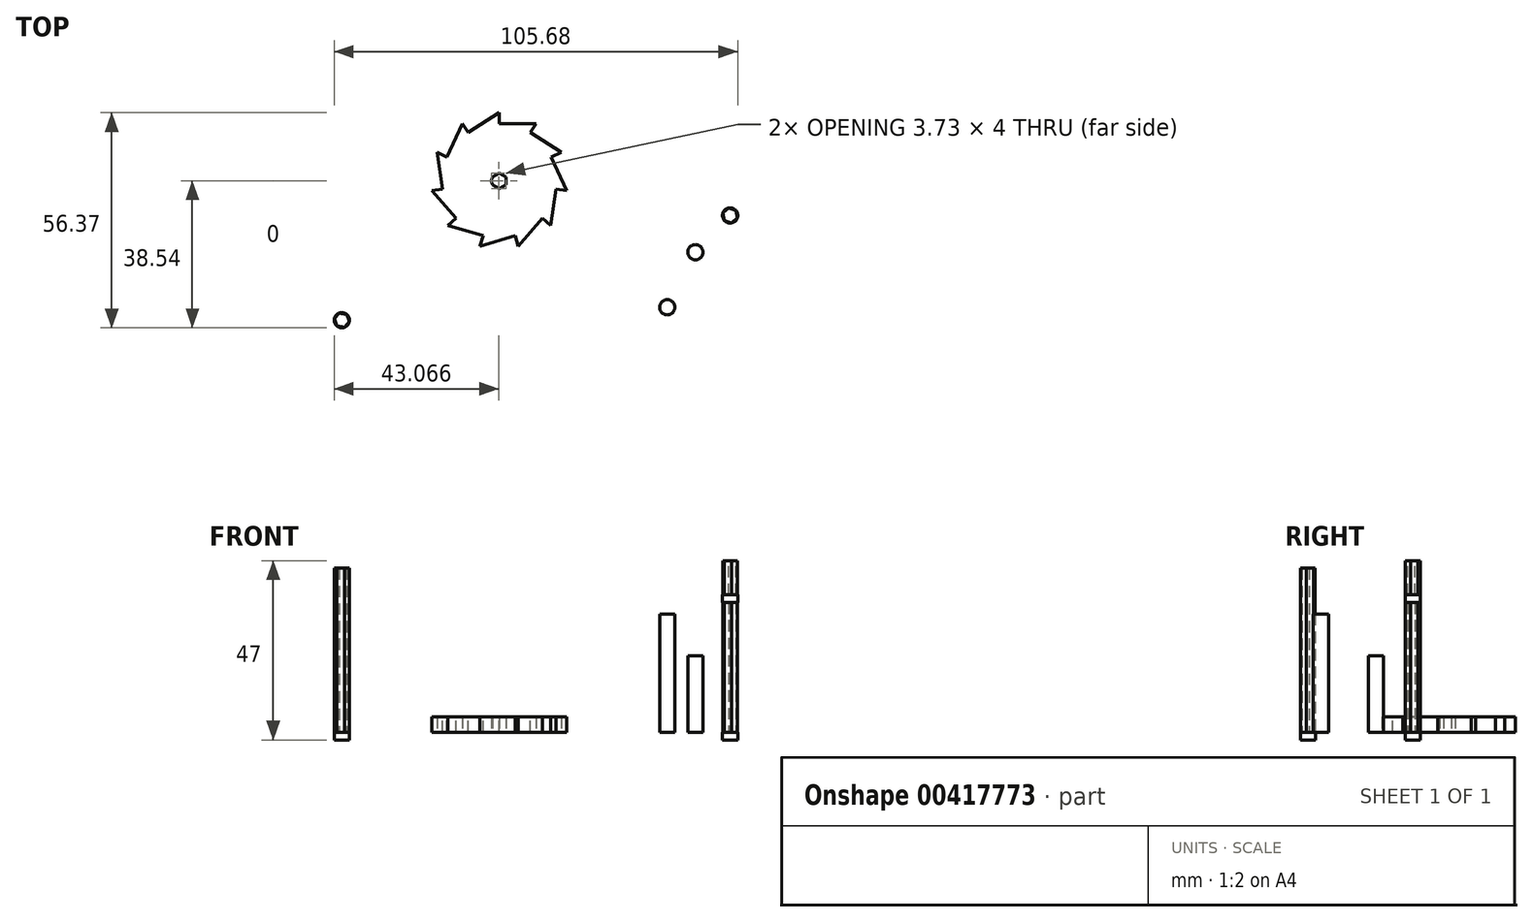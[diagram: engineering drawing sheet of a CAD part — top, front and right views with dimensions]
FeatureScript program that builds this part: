
annotation { "Feature Type Name" : "Feature", "Feature Type Description" : "" }
export const myFeature = defineFeature(function(context is Context, id is Id, definition is map)
    precondition{}
    {
        {
            var Q0;
            Q0=qCreatedBy(makeId("Top.planeOp"),FACE);
            var sketch = newSketch(context, id + "F0", { "sketchPlane" : qUnion([Q0])});
            skCircle(sketch, "E0", {"center": v(0, 0) * mm, "radius": 15 * mm});
            skLineSegment(sketch, "E1", {"start": v(0, -26.52) * mm, "end": v(0, 26.32) * mm});
            skLineSegment(sketch, "E2", {"start": v(-32.36, 0) * mm, "end": v(30.72, 0) * mm});
            skLineSegment(sketch, "E3", {"start": v(0, 15) * mm, "end": v(0, 17.83) * mm});
            skLineSegment(sketch, "E4", {"start": v(0, 17.83) * mm, "end": v(-8.1, 12.62) * mm});
            skLineSegment(sketch, "E5.1.0", {"start": v(-8.1, 12.62) * mm, "end": v(-9.64, 15) * mm});
            skLineSegment(sketch, "E5.1.1", {"start": v(-9.64, 15) * mm, "end": v(-13.64, 6.23) * mm});
            skLineSegment(sketch, "E5.2.0", {"start": v(-13.64, 6.23) * mm, "end": v(-16.22, 7.4) * mm});
            skLineSegment(sketch, "E5.2.1", {"start": v(-16.22, 7.4) * mm, "end": v(-14.85, -2.13) * mm});
            skLineSegment(sketch, "E5.3.0", {"start": v(-14.85, -2.13) * mm, "end": v(-17.65, -2.54) * mm});
            skLineSegment(sketch, "E5.3.1", {"start": v(-17.65, -2.54) * mm, "end": v(-11.34, -9.82) * mm});
            skLineSegment(sketch, "E5.4.0", {"start": v(-11.34, -9.82) * mm, "end": v(-13.48, -11.68) * mm});
            skLineSegment(sketch, "E5.4.1", {"start": v(-13.48, -11.68) * mm, "end": v(-4.23, -14.4) * mm});
            skLineSegment(sketch, "E5.5.0", {"start": v(-4.23, -14.4) * mm, "end": v(-5.02, -17.1) * mm});
            skLineSegment(sketch, "E5.5.1", {"start": v(-5.02, -17.1) * mm, "end": v(4.23, -14.4) * mm});
            skLineSegment(sketch, "E5.6.0", {"start": v(4.23, -14.4) * mm, "end": v(5.02, -17.1) * mm});
            skLineSegment(sketch, "E5.6.1", {"start": v(5.02, -17.1) * mm, "end": v(11.34, -9.82) * mm});
            skLineSegment(sketch, "E5.7.0", {"start": v(11.34, -9.82) * mm, "end": v(13.48, -11.68) * mm});
            skLineSegment(sketch, "E5.7.1", {"start": v(13.48, -11.68) * mm, "end": v(14.85, -2.13) * mm});
            skLineSegment(sketch, "E5.8.0", {"start": v(14.85, -2.13) * mm, "end": v(17.65, -2.54) * mm});
            skLineSegment(sketch, "E5.8.1", {"start": v(17.65, -2.54) * mm, "end": v(13.64, 6.23) * mm});
            skLineSegment(sketch, "E5.9.0", {"start": v(13.64, 6.23) * mm, "end": v(16.22, 7.4) * mm});
            skLineSegment(sketch, "E5.9.1", {"start": v(16.22, 7.4) * mm, "end": v(8.1, 12.62) * mm});
            skLineSegment(sketch, "E5.10.0", {"start": v(8.1, 12.62) * mm, "end": v(9.64, 15) * mm});
            skLineSegment(sketch, "E5.10.1", {"start": v(9.64, 15) * mm, "end": v(0, 15) * mm});
            skCircle(sketch, "E6.cCircle", {"center": v(0, 0) * mm, "radius": 1.73 * mm, "construction": true});
            skLineSegment(sketch, "E6.0", {"start": v(0, 2) * mm, "end": v(1.73, 1) * mm});
            skLineSegment(sketch, "E6.1", {"start": v(1.73, 1) * mm, "end": v(1.73, -1) * mm});
            skLineSegment(sketch, "E6.2", {"start": v(1.73, -1) * mm, "end": v(0, -2) * mm});
            skLineSegment(sketch, "E6.3", {"start": v(0, -2) * mm, "end": v(-1.73, -1) * mm});
            skLineSegment(sketch, "E6.4", {"start": v(-1.73, -1) * mm, "end": v(-1.73, 1) * mm});
            skLineSegment(sketch, "E6.5", {"start": v(-1.73, 1) * mm, "end": v(0, 2) * mm});
            skPoint(sketch, "E6.0.midPoint", {"position": v(0.87, 1.5) * mm});
            skCircle(sketch, "E7", {"center": v(0, 0) * mm, "radius": 2 * mm});
            skSolve(sketch);
        }
        {
            var Q0;
            Q0 = qSketchRegion(id + "F0", true);
            var Q1;
            {var subQ0=sQuery(id+"F0.wireOp",EDGE,"E6.5");Q1=makeQuery(id+"F0.imprint","IMPRINT",FACE,{"disambiguationData":[TD([[makeQuery(id+"F0.imprint","IMPRINT",EDGE,{"derivedFrom":subQ0}),1.0]])]});}
            var Q2;
            {var subQ0=sQuery(id+"F0.wireOp",EDGE,"E6.0");Q2=makeQuery(id+"F0.imprint","IMPRINT",FACE,{"disambiguationData":[TD([[makeQuery(id+"F0.imprint","IMPRINT",EDGE,{"derivedFrom":subQ0}),1.0]])]});}
            var Q3;
            {var subQ0=sQuery(id+"F0.wireOp",EDGE,"E6.1");var subQ1=sQuery(id+"F0.wireOp",EDGE,"E2");var subQ2=makeQuery(id+"F0.imprint","INTERSECT",VERTEX,{"derivedFrom":[subQ1,subQ0]});Q3=makeQuery(id+"F0.imprint","IMPRINT",FACE,{"disambiguationData":[TD([[makeQuery(id+"F0.imprint","IMPRINT",EDGE,{"disambiguationData":[TD([[subQ2,-1.0]])],"derivedFrom":subQ1}),1.0]])]});}
            var Q4;
            {var subQ0=sQuery(id+"F0.wireOp",EDGE,"E6.2");Q4=makeQuery(id+"F0.imprint","IMPRINT",FACE,{"disambiguationData":[TD([[makeQuery(id+"F0.imprint","IMPRINT",EDGE,{"derivedFrom":subQ0}),1.0]])]});}
            var Q5;
            {var subQ0=sQuery(id+"F0.wireOp",EDGE,"E6.3");Q5=makeQuery(id+"F0.imprint","IMPRINT",FACE,{"disambiguationData":[TD([[makeQuery(id+"F0.imprint","IMPRINT",EDGE,{"derivedFrom":subQ0}),1.0]])]});}
            var Q6;
            {var subQ0=sQuery(id+"F0.wireOp",EDGE,"E7");var subQ1=sQuery(id+"F0.wireOp",EDGE,"E2");var subQ2=makeQuery(id+"F0.imprint","INTERSECT",VERTEX,{"disambiguationData":[OD(0.0)],"derivedFrom":[subQ1,subQ0]});Q6=makeQuery(id+"F0.imprint","IMPRINT",FACE,{"disambiguationData":[TD([[makeQuery(id+"F0.imprint","IMPRINT",EDGE,{"disambiguationData":[TD([[subQ2,-1.0]])],"derivedFrom":subQ1}),1.0]])]});}
            var Q7;
            {var subQ0=sQuery(id+"F0.wireOp",EDGE,"E7");var subQ1=sQuery(id+"F0.wireOp",EDGE,"E2");var subQ2=makeQuery(id+"F0.imprint","INTERSECT",VERTEX,{"disambiguationData":[OD(0.0)],"derivedFrom":[subQ1,subQ0]});Q7=makeQuery(id+"F0.imprint","IMPRINT",FACE,{"disambiguationData":[TD([[makeQuery(id+"F0.imprint","IMPRINT",EDGE,{"disambiguationData":[TD([[subQ2,-1.0]])],"derivedFrom":subQ1}),-1.0]])]});}
            var Q8;
            {var subQ0=sQuery(id+"F0.wireOp",EDGE,"E6.1");var subQ1=sQuery(id+"F0.wireOp",EDGE,"E2");var subQ2=makeQuery(id+"F0.imprint","INTERSECT",VERTEX,{"derivedFrom":[subQ1,subQ0]});Q8=makeQuery(id+"F0.imprint","IMPRINT",FACE,{"disambiguationData":[TD([[makeQuery(id+"F0.imprint","IMPRINT",EDGE,{"disambiguationData":[TD([[subQ2,-1.0]])],"derivedFrom":subQ1}),-1.0]])]});}
            extrude(context, id + "F1", {"entities" : qUnion([Q0, Q1, Q2, Q3, Q4, Q5, Q6, Q7, Q8]), "depth" : 4 * mm});
        }
        {
            var Q0;
            Q0=qCreatedBy(makeId("Top.planeOp"),FACE);
            var sketch = newSketch(context, id + "F2", { "sketchPlane" : qUnion([Q0])});
            skCircle(sketch, "E8", {"center": v(44, -33.15) * mm, "radius": 2 * mm});
            skCircle(sketch, "E9", {"center": v(51.38, -18.72) * mm, "radius": 2 * mm});
            skCircle(sketch, "E10", {"center": v(60.48, -9.09) * mm, "radius": 2 * mm});
            skSolve(sketch);
        }
        {
            var Q0;
            Q0=makeQuery(id+"F2.imprint","IMPRINT",FACE,{"disambiguationData":[TD([[makeQuery(id+"F2.imprint","IMPRINT",EDGE,{"derivedFrom":sQuery(id+"F2.wireOp",EDGE,"E8")}),1.0]])]});
            extrude(context, id + "F3", {"entities" : qUnion([Q0]), "depth" : 31 * mm});
        }
        {
            var Q0;
            Q0=makeQuery(id+"F2.imprint","IMPRINT",FACE,{"disambiguationData":[TD([[makeQuery(id+"F2.imprint","IMPRINT",EDGE,{"derivedFrom":sQuery(id+"F2.wireOp",EDGE,"E9")}),1.0]])]});
            extrude(context, id + "F4", {"entities" : qUnion([Q0]), "depth" : 20 * mm});
        }
        {
            var Q0;
            Q0=makeQuery(id+"F2.imprint","IMPRINT",FACE,{"disambiguationData":[TD([[makeQuery(id+"F2.imprint","IMPRINT",EDGE,{"derivedFrom":sQuery(id+"F2.wireOp",EDGE,"E10")}),1.0]])]});
            extrude(context, id + "F5", {"entities" : qUnion([Q0]), "depth" : 45 * mm});
        }
        {
            var Q0;
            Q0=makeQuery(id+"F5.opExtrude","CAP_FACE",FACE,{"disambiguationData":[OSD([sQuery(id+"F2.wireOp",EDGE,"E10")])],"isStart":false});
            var sketch = newSketch(context, id + "F6", { "sketchPlane" : qUnion([Q0])});
            skCircle(sketch, "E11.cCircle", {"center": v(60.48, -9.09) * mm, "radius": 2 * mm, "construction": true});
            skLineSegment(sketch, "E11.0", {"start": v(60.07, -7.13) * mm, "end": v(61.97, -7.75) * mm});
            skLineSegment(sketch, "E11.1", {"start": v(61.97, -7.75) * mm, "end": v(62.38, -9.71) * mm});
            skLineSegment(sketch, "E11.2", {"start": v(62.38, -9.71) * mm, "end": v(60.88, -11.04) * mm});
            skLineSegment(sketch, "E11.3", {"start": v(60.88, -11.04) * mm, "end": v(58.98, -10.42) * mm});
            skLineSegment(sketch, "E11.4", {"start": v(58.98, -10.42) * mm, "end": v(58.58, -8.46) * mm});
            skLineSegment(sketch, "E11.5", {"start": v(58.58, -8.46) * mm, "end": v(60.07, -7.13) * mm});
            skSolve(sketch);
        }
        {
            var Q0;
            {var subQ0=sQuery(id+"F6.wireOp",EDGE,"E11.5");Q0=makeQuery(id+"F6.imprint","IMPRINT",FACE,{"disambiguationData":[TD([[makeQuery(id+"F6.imprint","IMPRINT",EDGE,{"derivedFrom":subQ0}),1.0]])]});}
            var Q1;
            {var subQ0=sQuery(id+"F6.wireOp",EDGE,"E11.0");Q1=makeQuery(id+"F6.imprint","IMPRINT",FACE,{"disambiguationData":[TD([[makeQuery(id+"F6.imprint","IMPRINT",EDGE,{"derivedFrom":subQ0}),1.0]])]});}
            var Q2;
            {var subQ0=sQuery(id+"F6.wireOp",EDGE,"E11.1");Q2=makeQuery(id+"F6.imprint","IMPRINT",FACE,{"disambiguationData":[TD([[makeQuery(id+"F6.imprint","IMPRINT",EDGE,{"derivedFrom":subQ0}),1.0]])]});}
            var Q3;
            {var subQ0=sQuery(id+"F6.wireOp",EDGE,"E11.2");Q3=makeQuery(id+"F6.imprint","IMPRINT",FACE,{"disambiguationData":[TD([[makeQuery(id+"F6.imprint","IMPRINT",EDGE,{"derivedFrom":subQ0}),1.0]])]});}
            var Q4;
            {var subQ0=sQuery(id+"F6.wireOp",EDGE,"E11.3");Q4=makeQuery(id+"F6.imprint","IMPRINT",FACE,{"disambiguationData":[TD([[makeQuery(id+"F6.imprint","IMPRINT",EDGE,{"derivedFrom":subQ0}),1.0]])]});}
            var Q5;
            {var subQ0=sQuery(id+"F6.wireOp",EDGE,"E11.4");Q5=makeQuery(id+"F6.imprint","IMPRINT",FACE,{"disambiguationData":[TD([[makeQuery(id+"F6.imprint","IMPRINT",EDGE,{"derivedFrom":subQ0}),1.0]])]});}
            extrude(context, id + "F7", {"entities" : qUnion([Q0, Q1, Q2, Q3, Q4, Q5]), "operationType" : NewBodyOperationType.REMOVE, "oppositeDirection" : true, "depth" : 9 * mm});
        }
        {
            var Q0;
            Q0=makeQuery(id+"F2.imprint","IMPRINT",FACE,{"disambiguationData":[TD([[makeQuery(id+"F2.imprint","IMPRINT",EDGE,{"derivedFrom":sQuery(id+"F2.wireOp",EDGE,"E10")}),1.0]])]});
            var sketch = newSketch(context, id + "F8", { "sketchPlane" : qUnion([Q0])});
            skCircle(sketch, "E12.cCircle", {"center": v(60.48, -9.09) * mm, "radius": 2 * mm, "construction": true});
            skLineSegment(sketch, "E12.0", {"start": v(61.97, -7.75) * mm, "end": v(62.38, -9.71) * mm});
            skLineSegment(sketch, "E12.1", {"start": v(62.38, -9.71) * mm, "end": v(60.88, -11.04) * mm});
            skLineSegment(sketch, "E12.2", {"start": v(60.88, -11.04) * mm, "end": v(58.98, -10.42) * mm});
            skLineSegment(sketch, "E12.3", {"start": v(58.98, -10.42) * mm, "end": v(58.58, -8.46) * mm});
            skLineSegment(sketch, "E12.4", {"start": v(58.58, -8.46) * mm, "end": v(60.07, -7.13) * mm});
            skLineSegment(sketch, "E12.5", {"start": v(60.07, -7.13) * mm, "end": v(61.97, -7.75) * mm});
            skSolve(sketch);
        }
        {
            var Q0;
            {var subQ0=sQuery(id+"F8.wireOp",EDGE,"E12.1");Q0=makeQuery(id+"F8.imprint","IMPRINT",FACE,{"disambiguationData":[TD([[makeQuery(id+"F8.imprint","IMPRINT",EDGE,{"derivedFrom":subQ0}),1.0]])]});}
            var Q1;
            {var subQ0=sQuery(id+"F8.wireOp",EDGE,"E12.0");Q1=makeQuery(id+"F8.imprint","IMPRINT",FACE,{"disambiguationData":[TD([[makeQuery(id+"F8.imprint","IMPRINT",EDGE,{"derivedFrom":subQ0}),1.0]])]});}
            var Q2;
            {var subQ0=sQuery(id+"F8.wireOp",EDGE,"E12.5");Q2=makeQuery(id+"F8.imprint","IMPRINT",FACE,{"disambiguationData":[TD([[makeQuery(id+"F8.imprint","IMPRINT",EDGE,{"derivedFrom":subQ0}),1.0]])]});}
            var Q3;
            {var subQ0=sQuery(id+"F8.wireOp",EDGE,"E12.4");Q3=makeQuery(id+"F8.imprint","IMPRINT",FACE,{"disambiguationData":[TD([[makeQuery(id+"F8.imprint","IMPRINT",EDGE,{"derivedFrom":subQ0}),1.0]])]});}
            var Q4;
            {var subQ0=sQuery(id+"F8.wireOp",EDGE,"E12.3");Q4=makeQuery(id+"F8.imprint","IMPRINT",FACE,{"disambiguationData":[TD([[makeQuery(id+"F8.imprint","IMPRINT",EDGE,{"derivedFrom":subQ0}),1.0]])]});}
            var Q5;
            {var subQ0=sQuery(id+"F8.wireOp",EDGE,"E12.2");Q5=makeQuery(id+"F8.imprint","IMPRINT",FACE,{"disambiguationData":[TD([[makeQuery(id+"F8.imprint","IMPRINT",EDGE,{"derivedFrom":subQ0}),1.0]])]});}
            extrude(context, id + "F9", {"entities" : qUnion([Q0, Q1, Q2, Q3, Q4, Q5]), "operationType" : NewBodyOperationType.REMOVE, "depth" : 34 * mm});
        }
        {
            var Q0;
            Q0=makeQuery(id+"F2.imprint","IMPRINT",FACE,{"disambiguationData":[TD([[makeQuery(id+"F2.imprint","IMPRINT",EDGE,{"derivedFrom":sQuery(id+"F2.wireOp",EDGE,"E10")}),1.0]])]});
            extrude(context, id + "F10", {"entities" : qUnion([Q0]), "operationType" : NewBodyOperationType.ADD, "oppositeDirection" : true, "depth" : 2 * mm});
        }
        {
            var Q0;
            Q0=qCreatedBy(makeId("Top.planeOp"),FACE);
            var sketch = newSketch(context, id + "F11", { "sketchPlane" : qUnion([Q0])});
            skCircle(sketch, "E13", {"center": v(-41.2, -36.54) * mm, "radius": 2 * mm});
            skCircle(sketch, "E14.cCircle", {"center": v(-41.2, -36.54) * mm, "radius": 2 * mm, "construction": true});
            skLineSegment(sketch, "E14.0", {"start": v(-41.85, -34.65) * mm, "end": v(-39.9, -35.02) * mm});
            skLineSegment(sketch, "E14.1", {"start": v(-39.9, -35.02) * mm, "end": v(-39.24, -36.91) * mm});
            skLineSegment(sketch, "E14.2", {"start": v(-39.24, -36.91) * mm, "end": v(-40.55, -38.43) * mm});
            skLineSegment(sketch, "E14.3", {"start": v(-40.55, -38.43) * mm, "end": v(-42.51, -38.05) * mm});
            skLineSegment(sketch, "E14.4", {"start": v(-42.51, -38.05) * mm, "end": v(-43.16, -36.16) * mm});
            skLineSegment(sketch, "E14.5", {"start": v(-43.16, -36.16) * mm, "end": v(-41.85, -34.65) * mm});
            skSolve(sketch);
        }
        {
            var Q0;
            Q0=makeQuery(id+"F11.imprint","IMPRINT",FACE,{"disambiguationData":[TD([[makeQuery(id+"F11.imprint","IMPRINT",EDGE,{"derivedFrom":sQuery(id+"F11.wireOp",EDGE,"E14.0")}),-1.0]])]});
            extrude(context, id + "F12", {"entities" : qUnion([Q0]), "depth" : 43 * mm});
        }
        {
            var Q0;
            Q0 = qSketchRegion(id + "F11", true);
            extrude(context, id + "F13", {"entities" : qUnion([Q0]), "operationType" : NewBodyOperationType.ADD, "oppositeDirection" : true, "depth" : 2 * mm});
        }
    });
